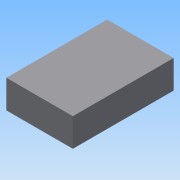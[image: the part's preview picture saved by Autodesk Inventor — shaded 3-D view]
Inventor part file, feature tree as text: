
AUTODESK INVENTOR PART (.ipt)
format: ipt  version: 2016 (Build 200138000, 138)  size: 136,704 bytes
history: native  units: mm
features: sketch x5, extrude x4, chamfer x1, plane x1, projected_geometry x1
ambient origin geometry x8: Origin, YZ Plane, XZ Plane, XY Plane, X Axis, Y Axis, Z Axis, Center Point
bodies: Volumenkörper1 (feature_tree)
feature tree (12):
  extrude  "Extrusion1"  Depth=250.0mm
  extrude  "Extrusion2"  Depth=70.0mm
  chamfer  "Fase1"  Distance=10.0mm
  sketch  "Skizze3"  dims[d5=35.0mm d6=10.0mm d7=0.0mm]
  plane  "Arbeitsebene1"
  extrude  "Extrusion3"  Depth=10.0mm
  extrude  "Extrusion4"  Depth=5.0mm
  sketch  "Skizze1"  dims[d0=165.0mm d1=250.0mm]
  sketch  "Skizze2"  dims[d2=70.0mm d3=0.0mm d4=105.0mm]
  sketch  "Skizze4"  dims[d8=30.0mm d9=2.0mm d10=60.0deg d11=10.0mm]
  sketch  "Skizze5"  dims[d12=-1.745329mm d13=230.0mm d14=140.0mm d15=25.0mm d16=0.0mm d17=110.0mm d18=200.0mm d19=30.0mm d20=5.0mm d21=0.0mm]
  projected_geometry  "Projizierte Kontur1"
